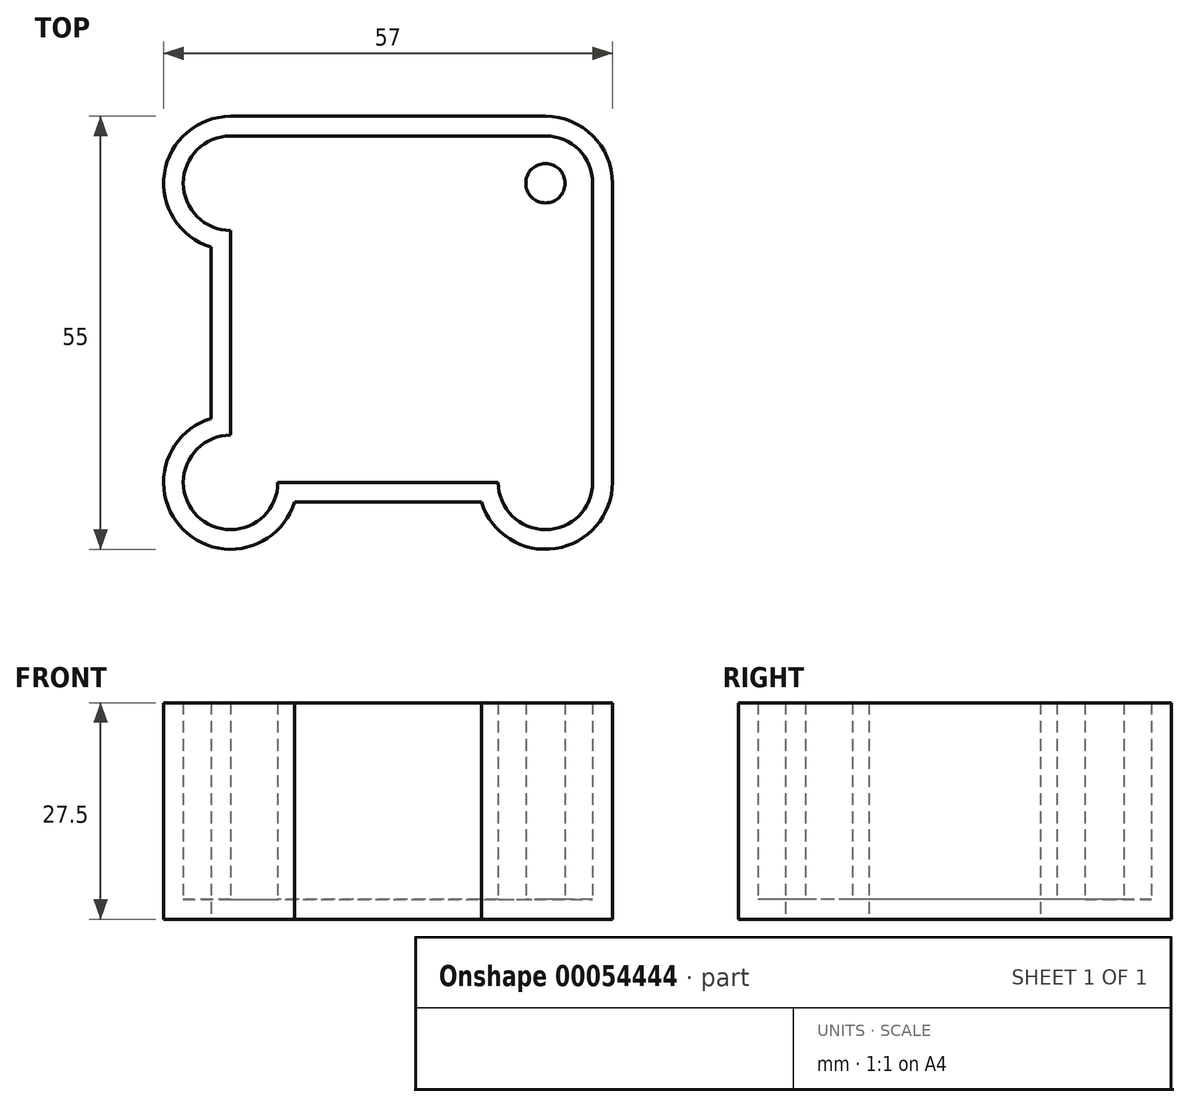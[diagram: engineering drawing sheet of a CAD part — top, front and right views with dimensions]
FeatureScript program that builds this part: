
annotation { "Feature Type Name" : "Feature", "Feature Type Description" : "" }
export const myFeature = defineFeature(function(context is Context, id is Id, definition is map)
    precondition{}
    {
        {
            var Q0;
            Q0=qCreatedBy(makeId("Top.planeOp"),FACE);
            var sketch = newSketch(context, id + "F0", { "sketchPlane" : qUnion([Q0])});
            skLineSegment(sketch, "E0.bottom", {"start": v(-148.28, 7.33) * mm, "end": v(-188.28, 7.33) * mm});
            skLineSegment(sketch, "E0.top", {"start": v(-148.28, -30.67) * mm, "end": v(-188.28, -30.67) * mm});
            skLineSegment(sketch, "E0.left", {"start": v(-148.28, 7.33) * mm, "end": v(-148.28, -30.67) * mm});
            skLineSegment(sketch, "E0.right", {"start": v(-188.28, 7.33) * mm, "end": v(-188.28, -30.67) * mm});
            skCircle(sketch, "E1", {"center": v(-188.28, 7.33) * mm, "radius": 2.5 * mm});
            skLineSegment(sketch, "E2", {"start": v(-168.28, 7.33) * mm, "end": v(-168.28, -30.67) * mm, "construction": true});
            skCircle(sketch, "E3.MirrorC", {"center": v(-148.28, 7.33) * mm, "radius": 2.5 * mm});
            skLineSegment(sketch, "E4", {"start": v(-188.28, -11.67) * mm, "end": v(-148.28, -11.67) * mm, "construction": true});
            skCircle(sketch, "E5.MirrorC", {"center": v(-148.28, -30.67) * mm, "radius": 2.5 * mm});
            skCircle(sketch, "E6.MirrorC", {"center": v(-188.28, -30.67) * mm, "radius": 2.5 * mm});
            skLineSegment(sketch, "E7.bottom", {"start": v(-194.28, 13.33) * mm, "end": v(-142.28, 13.33) * mm});
            skLineSegment(sketch, "E7.top", {"start": v(-194.28, -36.67) * mm, "end": v(-142.28, -36.67) * mm});
            skLineSegment(sketch, "E7.left", {"start": v(-194.28, 13.33) * mm, "end": v(-194.28, -36.67) * mm});
            skLineSegment(sketch, "E7.right", {"start": v(-142.28, 13.33) * mm, "end": v(-142.28, -36.67) * mm});
            skLineSegment(sketch, "E8", {"start": v(-148.28, -11.67) * mm, "end": v(-142.28, -11.67) * mm});
            skLineSegment(sketch, "E9", {"start": v(-168.28, 13.33) * mm, "end": v(-168.28, 7.33) * mm});
            skCircle(sketch, "E10", {"center": v(-188.28, -30.67) * mm, "radius": 6 * mm});
            skCircle(sketch, "E11.MirrorC", {"center": v(-148.28, -30.67) * mm, "radius": 6 * mm});
            skCircle(sketch, "E12.MirrorC", {"center": v(-188.28, 7.33) * mm, "radius": 6 * mm});
            skCircle(sketch, "E13.MirrorC", {"center": v(-148.28, 7.33) * mm, "radius": 6 * mm});
            skSolve(sketch);
        }
        {
            var Q0;
            {var subQ0=sQuery(id+"F0.wireOp",EDGE,"E4");var subQ1=sQuery(id+"F0.wireOp",EDGE,"E0.right");var subQ2=makeQuery(id+"F0.imprint","INTERSECT",VERTEX,{"derivedFrom":[subQ1,subQ0]});Q0=makeQuery(id+"F0.imprint","IMPRINT",FACE,{"disambiguationData":[TD([[makeQuery(id+"F0.imprint","IMPRINT",EDGE,{"disambiguationData":[TD([[subQ2,1.0]])],"derivedFrom":subQ1}),1.0]])]});}
            var Q1;
            {var subQ3=sQuery(id+"F0.wireOp",EDGE,"E2");var subQ5=sQuery(id+"F0.wireOp",EDGE,"E0.top");var subQ6=makeQuery(id+"F0.imprint","INTERSECT",VERTEX,{"derivedFrom":[subQ5,subQ3]});Q1=makeQuery(id+"F0.imprint","IMPRINT",FACE,{"disambiguationData":[TD([[makeQuery(id+"F0.imprint","IMPRINT",EDGE,{"disambiguationData":[TD([[subQ6,-1.0]])],"derivedFrom":subQ5}),-1.0]])]});}
            var Q2;
            {var subQ3=sQuery(id+"F0.wireOp",EDGE,"E2");var subQ5=sQuery(id+"F0.wireOp",EDGE,"E0.top");var subQ6=makeQuery(id+"F0.imprint","INTERSECT",VERTEX,{"derivedFrom":[subQ5,subQ3]});Q2=makeQuery(id+"F0.imprint","IMPRINT",FACE,{"disambiguationData":[TD([[makeQuery(id+"F0.imprint","IMPRINT",EDGE,{"disambiguationData":[TD([[subQ6,1.0]])],"derivedFrom":subQ5}),-1.0]])]});}
            var Q3;
            {var subQ5=sQuery(id+"F0.wireOp",EDGE,"E0.bottom");var subQ7=sQuery(id+"F0.wireOp",EDGE,"E13.MirrorC");var subQ9=makeQuery(id+"F0.imprint","INTERSECT",VERTEX,{"derivedFrom":[subQ5,subQ7]});Q3=makeQuery(id+"F0.imprint","IMPRINT",FACE,{"disambiguationData":[TD([[makeQuery(id+"F0.imprint","IMPRINT",EDGE,{"disambiguationData":[TD([[subQ9,-1.0]])],"derivedFrom":subQ7}),-1.0]])]});}
            var Q4;
            {var subQ3=sQuery(id+"F0.wireOp",EDGE,"E0.top");var subQ7=makeQuery(id+"F0.imprint","INTERSECT",VERTEX,{"derivedFrom":[subQ3,sQuery(id+"F0.wireOp",EDGE,"E2")]});Q4=makeQuery(id+"F0.imprint","IMPRINT",FACE,{"disambiguationData":[TD([[makeQuery(id+"F0.imprint","IMPRINT",EDGE,{"disambiguationData":[TD([[subQ7,1.0]])],"derivedFrom":subQ3}),1.0]])]});}
            var Q5;
            {var subQ3=sQuery(id+"F0.wireOp",EDGE,"E0.right");var subQ5=makeQuery(id+"F0.imprint","INTERSECT",VERTEX,{"derivedFrom":[subQ3,sQuery(id+"F0.wireOp",EDGE,"E4")]});Q5=makeQuery(id+"F0.imprint","IMPRINT",FACE,{"disambiguationData":[TD([[makeQuery(id+"F0.imprint","IMPRINT",EDGE,{"disambiguationData":[TD([[subQ5,1.0]])],"derivedFrom":subQ3}),-1.0]])]});}
            var Q6;
            {var subQ0=sQuery(id+"F0.wireOp",EDGE,"E10");var subQ5=sQuery(id+"F0.wireOp",EDGE,"E0.top");var subQ9=makeQuery(id+"F0.imprint","INTERSECT",VERTEX,{"derivedFrom":[subQ5,subQ0]});Q6=makeQuery(id+"F0.imprint","IMPRINT",FACE,{"disambiguationData":[TD([[makeQuery(id+"F0.imprint","IMPRINT",EDGE,{"disambiguationData":[TD([[subQ9,-1.0]])],"derivedFrom":subQ5}),1.0]])]});}
            var Q7;
            {var subQ0=sQuery(id+"F0.wireOp",EDGE,"E10");var subQ1=sQuery(id+"F0.wireOp",EDGE,"E0.top");var subQ2=makeQuery(id+"F0.imprint","INTERSECT",VERTEX,{"derivedFrom":[subQ1,subQ0]});Q7=makeQuery(id+"F0.imprint","IMPRINT",FACE,{"disambiguationData":[TD([[makeQuery(id+"F0.imprint","IMPRINT",EDGE,{"disambiguationData":[TD([[subQ2,-1.0]])],"derivedFrom":subQ1}),-1.0]])]});}
            var Q8;
            {var subQ0=sQuery(id+"F0.wireOp",EDGE,"E9");Q8=makeQuery(id+"F0.imprint","IMPRINT",FACE,{"disambiguationData":[TD([[makeQuery(id+"F0.imprint","IMPRINT",EDGE,{"derivedFrom":subQ0}),-1.0]])]});}
            var Q9;
            {var subQ0=sQuery(id+"F0.wireOp",EDGE,"E9");Q9=makeQuery(id+"F0.imprint","IMPRINT",FACE,{"disambiguationData":[TD([[makeQuery(id+"F0.imprint","IMPRINT",EDGE,{"derivedFrom":subQ0}),1.0]])]});}
            var Q10;
            {var subQ0=sQuery(id+"F0.wireOp",EDGE,"E8");Q10=makeQuery(id+"F0.imprint","IMPRINT",FACE,{"disambiguationData":[TD([[makeQuery(id+"F0.imprint","IMPRINT",EDGE,{"derivedFrom":subQ0}),1.0]])]});}
            var Q11;
            {var subQ0=sQuery(id+"F0.wireOp",EDGE,"E8");Q11=makeQuery(id+"F0.imprint","IMPRINT",FACE,{"disambiguationData":[TD([[makeQuery(id+"F0.imprint","IMPRINT",EDGE,{"derivedFrom":subQ0}),-1.0]])]});}
            var Q12;
            {var subQ4=sQuery(id+"F0.wireOp",EDGE,"E5.MirrorC");var subQ5=sQuery(id+"F0.wireOp",EDGE,"E0.top");var subQ6=makeQuery(id+"F0.imprint","INTERSECT",VERTEX,{"derivedFrom":[subQ5,subQ4]});Q12=makeQuery(id+"F0.imprint","IMPRINT",FACE,{"disambiguationData":[TD([[makeQuery(id+"F0.imprint","IMPRINT",EDGE,{"disambiguationData":[TD([[subQ6,-1.0]])],"derivedFrom":subQ5}),1.0]])]});}
            var Q13;
            {var subQ0=sQuery(id+"F0.wireOp",EDGE,"E5.MirrorC");var subQ1=sQuery(id+"F0.wireOp",EDGE,"E0.top");var subQ2=makeQuery(id+"F0.imprint","INTERSECT",VERTEX,{"derivedFrom":[subQ1,subQ0]});Q13=makeQuery(id+"F0.imprint","IMPRINT",FACE,{"disambiguationData":[TD([[makeQuery(id+"F0.imprint","IMPRINT",EDGE,{"disambiguationData":[TD([[subQ2,-1.0]])],"derivedFrom":subQ1}),-1.0]])]});}
            var Q14;
            {var subQ4=sQuery(id+"F0.wireOp",EDGE,"E3.MirrorC");var subQ5=sQuery(id+"F0.wireOp",EDGE,"E0.bottom");var subQ6=makeQuery(id+"F0.imprint","INTERSECT",VERTEX,{"derivedFrom":[subQ5,subQ4]});Q14=makeQuery(id+"F0.imprint","IMPRINT",FACE,{"disambiguationData":[TD([[makeQuery(id+"F0.imprint","IMPRINT",EDGE,{"disambiguationData":[TD([[subQ6,-1.0]])],"derivedFrom":subQ5}),-1.0]])]});}
            var Q15;
            {var subQ0=sQuery(id+"F0.wireOp",EDGE,"E3.MirrorC");var subQ1=sQuery(id+"F0.wireOp",EDGE,"E0.bottom");var subQ2=makeQuery(id+"F0.imprint","INTERSECT",VERTEX,{"derivedFrom":[subQ1,subQ0]});Q15=makeQuery(id+"F0.imprint","IMPRINT",FACE,{"disambiguationData":[TD([[makeQuery(id+"F0.imprint","IMPRINT",EDGE,{"disambiguationData":[TD([[subQ2,-1.0]])],"derivedFrom":subQ1}),1.0]])]});}
            var Q16;
            {var subQ0=sQuery(id+"F0.wireOp",EDGE,"E12.MirrorC");var subQ1=sQuery(id+"F0.wireOp",EDGE,"E0.bottom");var subQ2=makeQuery(id+"F0.imprint","INTERSECT",VERTEX,{"derivedFrom":[subQ1,subQ0]});Q16=makeQuery(id+"F0.imprint","IMPRINT",FACE,{"disambiguationData":[TD([[makeQuery(id+"F0.imprint","IMPRINT",EDGE,{"disambiguationData":[TD([[subQ2,-1.0]])],"derivedFrom":subQ1}),1.0]])]});}
            var Q17;
            {var subQ0=sQuery(id+"F0.wireOp",EDGE,"E12.MirrorC");var subQ5=sQuery(id+"F0.wireOp",EDGE,"E0.bottom");var subQ9=makeQuery(id+"F0.imprint","INTERSECT",VERTEX,{"derivedFrom":[subQ5,subQ0]});Q17=makeQuery(id+"F0.imprint","IMPRINT",FACE,{"disambiguationData":[TD([[makeQuery(id+"F0.imprint","IMPRINT",EDGE,{"disambiguationData":[TD([[subQ9,-1.0]])],"derivedFrom":subQ5}),-1.0]])]});}
            extrude(context, id + "F1", {"entities" : qUnion([Q0, Q1, Q2, Q3, Q4, Q5, Q6, Q7, Q8, Q9, Q10, Q11, Q12, Q13, Q14, Q15, Q16, Q17]), "depth" : 25 * mm});
        }
        {
            var Q0;
            Q0=makeQuery(id+"F1.opExtrude","CAP_FACE",FACE,{"disambiguationData":[OSD([sQuery(id+"F0.wireOp",EDGE,"E1"),sQuery(id+"F0.wireOp",EDGE,"E3.MirrorC"),sQuery(id+"F0.wireOp",EDGE,"E5.MirrorC"),sQuery(id+"F0.wireOp",EDGE,"E6.MirrorC"),sQuery(id+"F0.wireOp",EDGE,"E7.bottom"),sQuery(id+"F0.wireOp",EDGE,"E7.top"),sQuery(id+"F0.wireOp",EDGE,"E7.left"),sQuery(id+"F0.wireOp",EDGE,"E7.right"),sQuery(id+"F0.wireOp",EDGE,"E10"),sQuery(id+"F0.wireOp",EDGE,"E11.MirrorC"),sQuery(id+"F0.wireOp",EDGE,"E12.MirrorC"),sQuery(id+"F0.wireOp",EDGE,"E13.MirrorC")])],"isStart":false});
            shell(context, id + "F2", {"entities" : qUnion([Q0]), "thickness" : 2.5 * mm, "oppositeDirection" : true});
        }
    });
